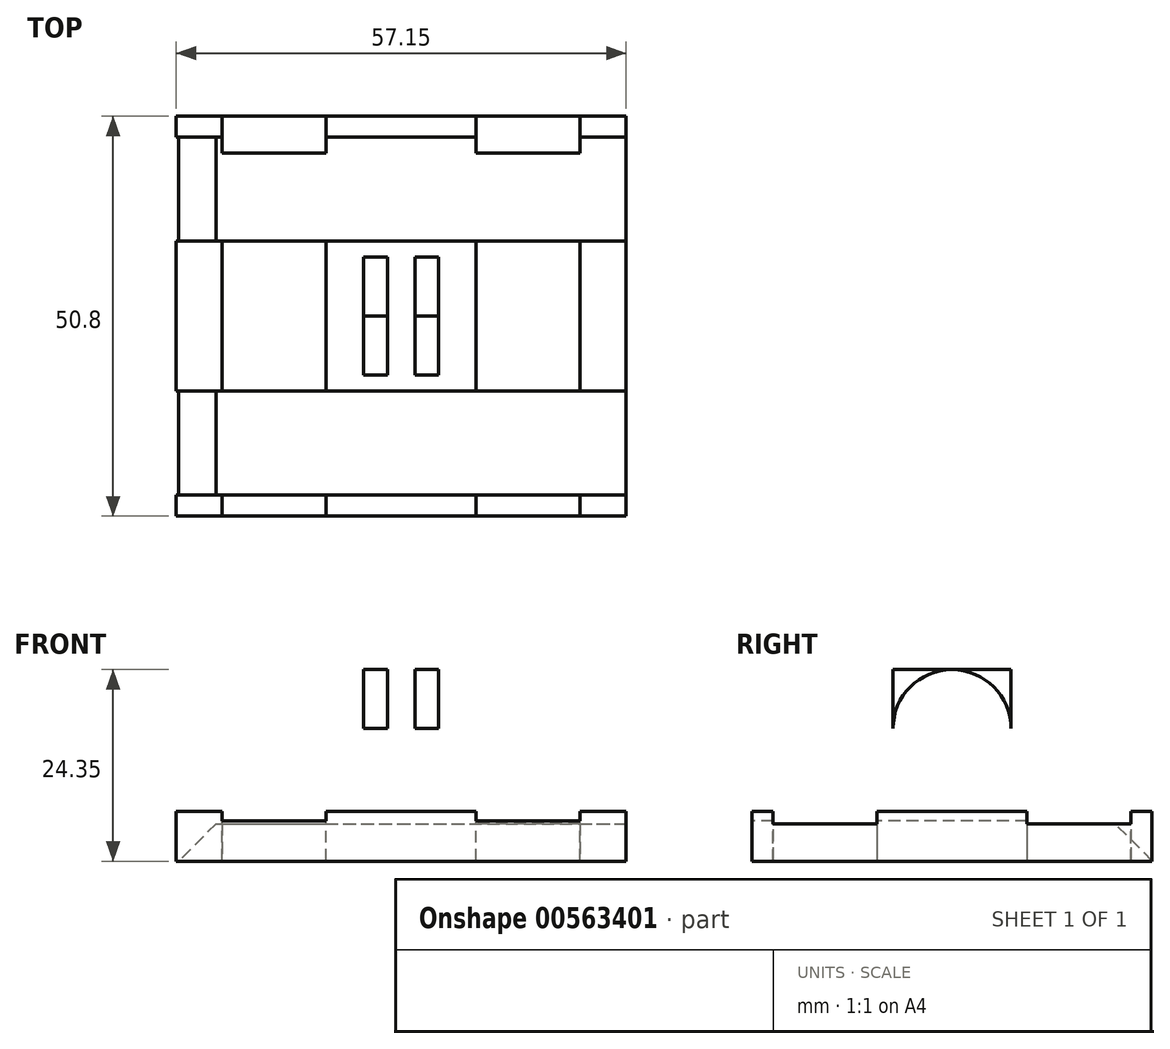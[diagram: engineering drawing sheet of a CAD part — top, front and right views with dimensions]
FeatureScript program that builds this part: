
annotation { "Feature Type Name" : "Feature", "Feature Type Description" : "" }
export const myFeature = defineFeature(function(context is Context, id is Id, definition is map)
    precondition{}
    {
        {
            var Q0;
            Q0=qCreatedBy(makeId("Top.planeOp"),FACE);
            var sketch = newSketch(context, id + "F0", { "sketchPlane" : qUnion([Q0])});
            skLineSegment(sketch, "E0.bottom", {"start": v(-28.58, 25.4) * mm, "end": v(28.58, 25.4) * mm});
            skLineSegment(sketch, "E0.top", {"start": v(-28.58, -25.4) * mm, "end": v(28.58, -25.4) * mm});
            skLineSegment(sketch, "E0.left", {"start": v(-28.57, 25.4) * mm, "end": v(-28.58, -25.4) * mm});
            skLineSegment(sketch, "E0.right", {"start": v(28.58, 25.4) * mm, "end": v(28.57, -25.4) * mm});
            skPoint(sketch, "E0.middle", {"position": v(0, 0) * mm});
            skSolve(sketch);
        }
        {
            var Q0;
            Q0=makeQuery(id+"F0.imprint","IMPRINT",FACE,{"disambiguationData":[TD([[makeQuery(id+"F0.imprint","IMPRINT",EDGE,{"derivedFrom":sQuery(id+"F0.wireOp",EDGE,"E0.bottom")}),-1.0]])]});
            extrude(context, id + "F1", {"entities" : qUnion([Q0]), "depth" : 6.35 * mm, "offsetDistance" : 25.4 * mm});
        }
        {
            var Q0;
            Q0=makeQuery(id+"FtcuCWjjDslHPHS_1.boolean.opBoolean","MERGE",FACE,{"derivedFrom":[makeQuery(id+"F1.opExtrude","SWEPT_FACE",FACE,{"disambiguationData":[OSD([sQuery(id+"F0.wireOp",EDGE,"E0.top")])]}),makeQuery(id+"FtcuCWjjDslHPHS_1.opExtrude","SWEPT_FACE",FACE,{"disambiguationData":[OSD([sQuery(id+"FMVw0hR87RWjdVx_1.wireOp",EDGE,"ffXjeifS-v08F-Zf74-KwMz-o1rhuZgXpIRW.top")])]}),makeQuery(id+"FtcuCWjjDslHPHS_1.opExtrude","SWEPT_FACE",FACE,{"disambiguationData":[OSD([sQuery(id+"FMVw0hR87RWjdVx_1.wireOp",EDGE,"9689fe90-bb07-47c0-8046-fc975a32ab120.MirrorCS")])]})]});
            var sketch = newSketch(context, id + "F2", { "sketchPlane" : qUnion([Q0])});
            skLineSegment(sketch, "E1.bottom", {"start": v(-22.73, 6.35) * mm, "end": v(-9.53, 6.35) * mm});
            skLineSegment(sketch, "E1.top", {"start": v(-22.73, 5.16) * mm, "end": v(-9.53, 5.16) * mm});
            skLineSegment(sketch, "E1.left", {"start": v(-22.73, 6.35) * mm, "end": v(-22.73, 5.16) * mm});
            skLineSegment(sketch, "E1.right", {"start": v(-9.53, 6.35) * mm, "end": v(-9.53, 5.16) * mm});
            skLineSegment(sketch, "E2.MirrorCS", {"start": v(9.53, 6.35) * mm, "end": v(9.53, 5.16) * mm});
            skLineSegment(sketch, "E3.MirrorCS", {"start": v(22.73, 6.35) * mm, "end": v(9.53, 6.35) * mm});
            skLineSegment(sketch, "E4.MirrorCS", {"start": v(22.73, 6.35) * mm, "end": v(22.73, 5.16) * mm});
            skLineSegment(sketch, "E5.MirrorCS", {"start": v(22.73, 5.16) * mm, "end": v(9.53, 5.16) * mm});
            skSolve(sketch);
        }
        {
            var Q0;
            Q0 = qSketchRegion(id + "F2", true);
            extrude(context, id + "F3", {"entities" : qUnion([Q0]), "operationType" : NewBodyOperationType.REMOVE, "endBound" : BoundingType.THROUGH_ALL, "oppositeDirection" : true, "depth" : 25.4 * mm, "offsetDistance" : 25.4 * mm});
        }
        {
            var Q0;
            Q0=makeQuery(id+"F3.boolean.opBoolean","COPY",EDGE,{"derivedFrom":makeQuery(id+"F3.opExtrude","CAP_EDGE",EDGE,{"disambiguationData":[OSD([sQuery(id+"F2.wireOp",EDGE,"E1.top")])],"isStart":true})});
            var Q1;
            Q1=makeQuery(id+"F3.boolean.opBoolean","INTERSECT",EDGE,{"derivedFrom":[makeQuery(id+"FtcuCWjjDslHPHS_1.boolean.opBoolean","MERGE",FACE,{"derivedFrom":[makeQuery(id+"F1.opExtrude","SWEPT_FACE",FACE,{"disambiguationData":[OSD([sQuery(id+"F0.wireOp",EDGE,"E0.bottom")])]}),makeQuery(id+"FtcuCWjjDslHPHS_1.opExtrude","SWEPT_FACE",FACE,{"disambiguationData":[OSD([sQuery(id+"FMVw0hR87RWjdVx_1.wireOp",EDGE,"ffXjeifS-v08F-Zf74-KwMz-o1rhuZgXpIRW.bottom")])]}),makeQuery(id+"FtcuCWjjDslHPHS_1.opExtrude","SWEPT_FACE",FACE,{"disambiguationData":[OSD([sQuery(id+"FMVw0hR87RWjdVx_1.wireOp",EDGE,"d3afc862-6923-4452-8843-25e1cdd5f01b0.MirrorCS")])]})]}),makeQuery(id+"F3.opExtrude","SWEPT_FACE",FACE,{"disambiguationData":[OSD([sQuery(id+"F2.wireOp",EDGE,"E1.top")])]})]});
            var Q2;
            Q2=makeQuery(id+"F3.boolean.opBoolean","COPY",EDGE,{"derivedFrom":makeQuery(id+"F3.opExtrude","CAP_EDGE",EDGE,{"disambiguationData":[OSD([sQuery(id+"F2.wireOp",EDGE,"E5.MirrorCS")])],"isStart":true})});
            var Q3;
            Q3=makeQuery(id+"F3.boolean.opBoolean","INTERSECT",EDGE,{"derivedFrom":[makeQuery(id+"FtcuCWjjDslHPHS_1.boolean.opBoolean","MERGE",FACE,{"derivedFrom":[makeQuery(id+"F1.opExtrude","SWEPT_FACE",FACE,{"disambiguationData":[OSD([sQuery(id+"F0.wireOp",EDGE,"E0.bottom")])]}),makeQuery(id+"FtcuCWjjDslHPHS_1.opExtrude","SWEPT_FACE",FACE,{"disambiguationData":[OSD([sQuery(id+"FMVw0hR87RWjdVx_1.wireOp",EDGE,"ffXjeifS-v08F-Zf74-KwMz-o1rhuZgXpIRW.bottom")])]}),makeQuery(id+"FtcuCWjjDslHPHS_1.opExtrude","SWEPT_FACE",FACE,{"disambiguationData":[OSD([sQuery(id+"FMVw0hR87RWjdVx_1.wireOp",EDGE,"d3afc862-6923-4452-8843-25e1cdd5f01b0.MirrorCS")])]})]}),makeQuery(id+"F3.opExtrude","SWEPT_FACE",FACE,{"disambiguationData":[OSD([sQuery(id+"F2.wireOp",EDGE,"E5.MirrorCS")])]})]});
            chamfer(context, id + "F4", {"entities" : qUnion([Q0, Q1, Q2, Q3]), "width" : 5.08 * mm, "tangentPropagation" : true});
        }
        {
            var Q0;
            {var subQ0=sQuery(id+"F0.wireOp",EDGE,"E0.bottom");var subQ1=sQuery(id+"F0.wireOp",EDGE,"E0.top");Q0=makeQuery(id+"F3.boolean.opBoolean","SPLIT",FACE,{"disambiguationData":[TD([makeQuery(id+"F3.opExtrude","SWEPT_FACE",FACE,{"disambiguationData":[OSD([sQuery(id+"F2.wireOp",EDGE,"E1.right")])]})])],"derivedFrom":makeQuery(id+"F1.opExtrude","CAP_FACE",FACE,{"disambiguationData":[OSD([subQ0,subQ1,sQuery(id+"F0.wireOp",EDGE,"E0.left"),sQuery(id+"F0.wireOp",EDGE,"E0.right")])],"isStart":false})});}
            var sketch = newSketch(context, id + "F5", { "sketchPlane" : qUnion([Q0])});
            skLineSegment(sketch, "E6.bottom", {"start": v(-4.75, 7.5) * mm, "end": v(-1.75, 7.5) * mm});
            skLineSegment(sketch, "E6.top", {"start": v(-4.75, -7.5) * mm, "end": v(-1.75, -7.5) * mm});
            skLineSegment(sketch, "E6.left", {"start": v(-4.75, 7.5) * mm, "end": v(-4.75, -7.5) * mm});
            skLineSegment(sketch, "E6.right", {"start": v(-1.75, 7.5) * mm, "end": v(-1.75, -7.5) * mm});
            skPoint(sketch, "E6.middle", {"position": v(-3.25, 0) * mm});
            skLineSegment(sketch, "E7.MirrorCS", {"start": v(4.75, 7.5) * mm, "end": v(1.75, 7.5) * mm});
            skLineSegment(sketch, "E8.MirrorCS", {"start": v(4.75, 7.5) * mm, "end": v(4.75, -7.5) * mm});
            skLineSegment(sketch, "E9.MirrorCS", {"start": v(1.75, 7.5) * mm, "end": v(1.75, -7.5) * mm});
            skLineSegment(sketch, "E10.MirrorCS", {"start": v(4.75, -7.5) * mm, "end": v(1.75, -7.5) * mm});
            skSolve(sketch);
        }
        {
            var Q0;
            Q0 = qSketchRegion(id + "F5", true);
            extrude(context, id + "F6", {"entities" : qUnion([Q0]), "operationType" : NewBodyOperationType.ADD, "depth" : 18 * mm, "offsetDistance" : 25.4 * mm});
        }
        {
            var Q0;
            Q0=makeQuery(id+"F6.opExtrude","SWEPT_FACE",FACE,{"disambiguationData":[OSD([sQuery(id+"F5.wireOp",EDGE,"E8.MirrorCS")])]});
            var sketch = newSketch(context, id + "F7", { "sketchPlane" : qUnion([Q0])});
            skPoint(sketch, "E11", {"position": v(0, 16.85) * mm});
            skSolve(sketch);
        }
        {
            var Q0;
            Q0=sQuery(id+"F7.wireOp",VERTEX,"E11");
            var Q1;
            Q1=makeQuery(id+"F1.opExtrude","SWEPT_BODY",BODY,{"disambiguationData":[OSD([sQuery(id+"F0.wireOp",EDGE,"E0.bottom"),sQuery(id+"F0.wireOp",EDGE,"E0.top"),sQuery(id+"F0.wireOp",EDGE,"E0.left"),sQuery(id+"F0.wireOp",EDGE,"E0.right")])]});
            hole(context, id + "F8", {"style" : HoleStyle.SIMPLE, "endStyle" : HoleEndStyle.THROUGH, "holeDiameter" : 5 * mm, "isTappedThrough" : true, "tappedDepth" : 12.7 * mm, "tapClearance" : 3, "locations" : qUnion([Q0]), "scope" : qUnion([Q1])});
        }
        {
            var Q0;
            Q0=makeQuery(id+"F1.opExtrude","SWEPT_FACE",FACE,{"disambiguationData":[OSD([sQuery(id+"F0.wireOp",EDGE,"E0.right")])]});
            var sketch = newSketch(context, id + "F9", { "sketchPlane" : qUnion([Q0])});
            skLineSegment(sketch, "E12.bottom", {"start": v(-22.73, 6.35) * mm, "end": v(-9.52, 6.35) * mm});
            skLineSegment(sketch, "E12.top", {"start": v(-22.73, 4.76) * mm, "end": v(-9.52, 4.76) * mm});
            skLineSegment(sketch, "E12.left", {"start": v(-22.73, 6.35) * mm, "end": v(-22.73, 4.76) * mm});
            skLineSegment(sketch, "E12.right", {"start": v(-9.52, 6.35) * mm, "end": v(-9.52, 4.76) * mm});
            skLineSegment(sketch, "E13.MirrorCS", {"start": v(9.53, 6.35) * mm, "end": v(9.53, 4.76) * mm});
            skLineSegment(sketch, "E14.MirrorCS", {"start": v(22.73, 6.35) * mm, "end": v(9.53, 6.35) * mm});
            skLineSegment(sketch, "E15.MirrorCS", {"start": v(22.73, 6.35) * mm, "end": v(22.73, 4.76) * mm});
            skLineSegment(sketch, "E16.MirrorCS", {"start": v(22.73, 4.76) * mm, "end": v(9.53, 4.76) * mm});
            skSolve(sketch);
        }
        {
            var Q0;
            Q0 = qSketchRegion(id + "F9", true);
            extrude(context, id + "F10", {"entities" : qUnion([Q0]), "operationType" : NewBodyOperationType.REMOVE, "endBound" : BoundingType.THROUGH_ALL, "oppositeDirection" : true, "depth" : 25.4 * mm, "offsetDistance" : 25.4 * mm});
        }
        {
            var Q0;
            Q0=makeQuery(id+"F10.boolean.opBoolean","COPY",EDGE,{"derivedFrom":makeQuery(id+"F10.opExtrude","CAP_EDGE",EDGE,{"disambiguationData":[OSD([sQuery(id+"F9.wireOp",EDGE,"E16.MirrorCS")])],"isStart":true})});
            var Q1;
            Q1=makeQuery(id+"F10.boolean.opBoolean","COPY",EDGE,{"derivedFrom":makeQuery(id+"F10.opExtrude","CAP_EDGE",EDGE,{"disambiguationData":[OSD([sQuery(id+"F9.wireOp",EDGE,"E12.top")])],"isStart":true})});
            var Q2;
            Q2=makeQuery(id+"F10.boolean.opBoolean","INTERSECT",EDGE,{"derivedFrom":[makeQuery(id+"F1.opExtrude","SWEPT_FACE",FACE,{"disambiguationData":[OSD([sQuery(id+"F0.wireOp",EDGE,"E0.left")])]}),makeQuery(id+"F10.opExtrude","SWEPT_FACE",FACE,{"disambiguationData":[OSD([sQuery(id+"F9.wireOp",EDGE,"E16.MirrorCS")])]})]});
            var Q3;
            Q3=makeQuery(id+"F10.boolean.opBoolean","INTERSECT",EDGE,{"derivedFrom":[makeQuery(id+"F1.opExtrude","SWEPT_FACE",FACE,{"disambiguationData":[OSD([sQuery(id+"F0.wireOp",EDGE,"E0.left")])]}),makeQuery(id+"F10.opExtrude","SWEPT_FACE",FACE,{"disambiguationData":[OSD([sQuery(id+"F9.wireOp",EDGE,"E12.top")])]})]});
            chamfer(context, id + "F11", {"entities" : qUnion([Q0, Q1, Q2, Q3]), "width" : 5.08 * mm, "tangentPropagation" : true});
        }
        {
            var Q0;
            Q0=makeQuery(id+"F6.opExtrude","SWEPT_FACE",FACE,{"disambiguationData":[OSD([sQuery(id+"F5.wireOp",EDGE,"E6.left")])]});
            var sketch = newSketch(context, id + "F12", { "sketchPlane" : qUnion([Q0])});
            skArc(sketch, "E17", {"start": v(-7.5, 16.85) * mm, "mid": v(0, 24.35) * mm, "end": v(7.5, 16.85) * mm});
            skSolve(sketch);
        }
        {
            var Q0;
            {var subQ0=sQuery(id+"F12.wireOp",EDGE,"E17");var subQ1=sQuery(id+"F5.wireOp",EDGE,"E6.left");var subQ4=makeQuery(id+"F6.opExtrude","CAP_EDGE",EDGE,{"disambiguationData":[OSD([subQ1])],"isStart":false});var subQ5=makeQuery(id+"F12.imprint","INTERSECT",VERTEX,{"disambiguationData":[OD(0.0)],"derivedFrom":[subQ4,subQ0]});Q0=makeQuery(id+"F12.imprint","IMPRINT",FACE,{"disambiguationData":[TD([[makeQuery(id+"F12.imprint","IMPRINT",EDGE,{"disambiguationData":[TD([[subQ5,1.0]])],"derivedFrom":subQ0}),1.0]])]});}
            var Q1;
            {var subQ0=sQuery(id+"F12.wireOp",EDGE,"E17");var subQ1=sQuery(id+"F5.wireOp",EDGE,"E6.left");var subQ4=makeQuery(id+"F6.opExtrude","CAP_EDGE",EDGE,{"disambiguationData":[OSD([subQ1])],"isStart":false});var subQ5=makeQuery(id+"F12.imprint","INTERSECT",VERTEX,{"disambiguationData":[OD(1.0)],"derivedFrom":[subQ4,subQ0]});Q1=makeQuery(id+"F12.imprint","IMPRINT",FACE,{"disambiguationData":[TD([[makeQuery(id+"F12.imprint","IMPRINT",EDGE,{"disambiguationData":[TD([[subQ5,-1.0]])],"derivedFrom":subQ0}),1.0]])]});}
            extrude(context, id + "F13", {"entities" : qUnion([Q0, Q1]), "operationType" : NewBodyOperationType.REMOVE, "endBound" : BoundingType.THROUGH_ALL, "oppositeDirection" : true, "depth" : 25.4 * mm, "offsetDistance" : 25.4 * mm});
        }
    });
